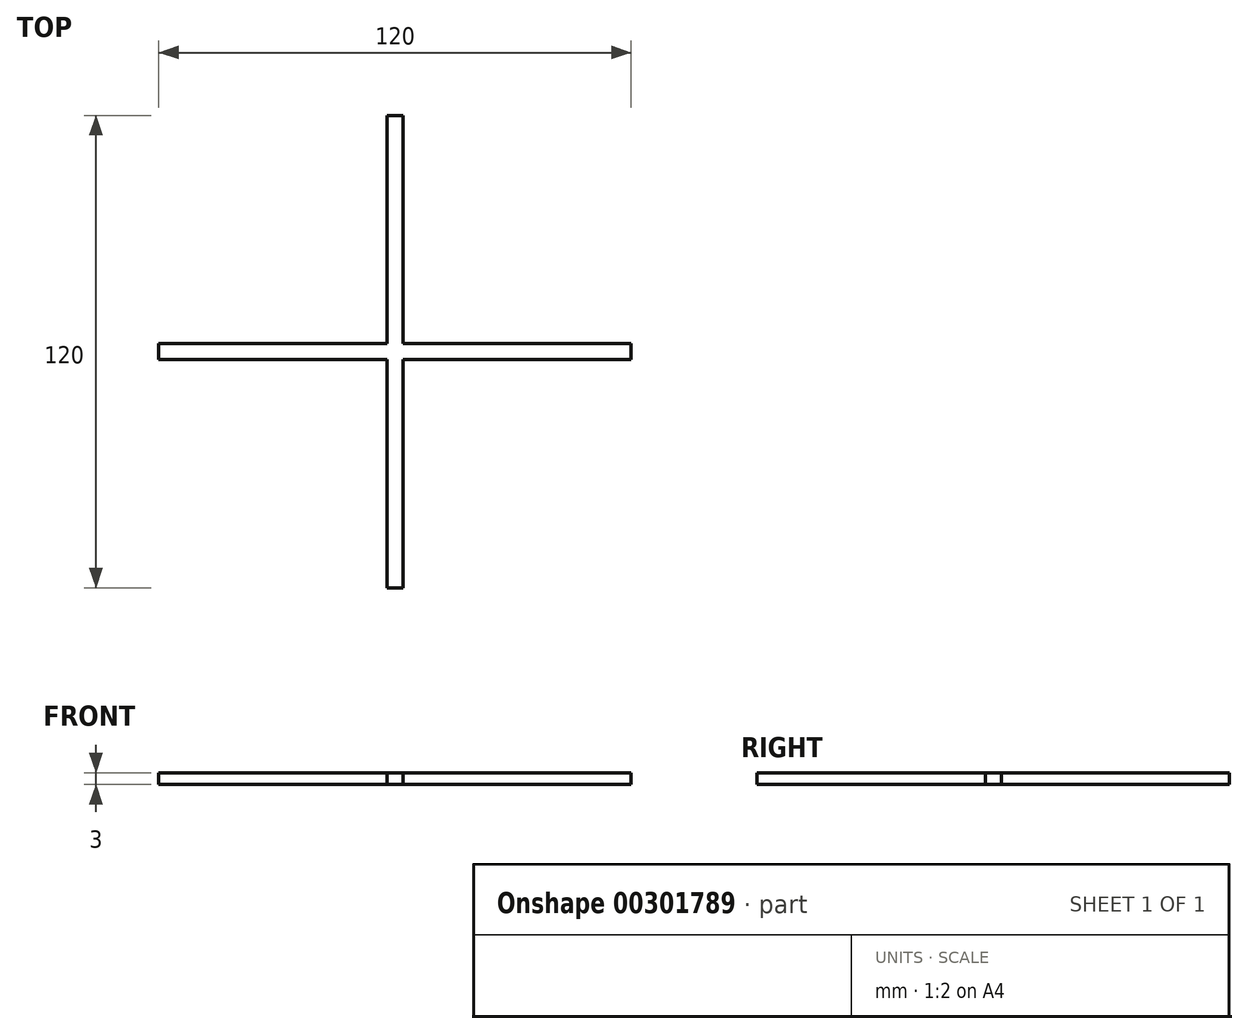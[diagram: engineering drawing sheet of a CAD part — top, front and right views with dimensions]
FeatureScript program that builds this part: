
annotation { "Feature Type Name" : "Feature", "Feature Type Description" : "" }
export const myFeature = defineFeature(function(context is Context, id is Id, definition is map)
    precondition{}
    {
        {
            var Q0;
            Q0=qCreatedBy(makeId("Top.planeOp"),FACE);
            var sketch = newSketch(context, id + "F0", { "sketchPlane" : qUnion([Q0])});
            skLineSegment(sketch, "E0.bottom", {"start": v(2, -60) * mm, "end": v(-2, -60) * mm});
            skLineSegment(sketch, "E0.top", {"start": v(2, 60) * mm, "end": v(-2, 60) * mm});
            skLineSegment(sketch, "E0.left", {"start": v(2, -60) * mm, "end": v(2, 60) * mm});
            skLineSegment(sketch, "E0.right", {"start": v(-2, -60) * mm, "end": v(-2, 60) * mm});
            skPoint(sketch, "E0.middle", {"position": v(0, 0) * mm});
            skLineSegment(sketch, "E1.bottom", {"start": v(60, -2) * mm, "end": v(-60, -2) * mm});
            skLineSegment(sketch, "E1.top", {"start": v(60, 2) * mm, "end": v(-60, 2) * mm});
            skLineSegment(sketch, "E1.left", {"start": v(60, -2) * mm, "end": v(60, 2) * mm});
            skLineSegment(sketch, "E1.right", {"start": v(-60, -2) * mm, "end": v(-60, 2) * mm});
            skSolve(sketch);
        }
        {
            var Q0;
            {var subQ5=sQuery(id+"F0.wireOp",EDGE,"E1.right");Q0=makeQuery(id+"F0.imprint","IMPRINT",FACE,{"disambiguationData":[TD([[makeQuery(id+"F0.imprint","IMPRINT",EDGE,{"derivedFrom":subQ5}),-1.0]])]});}
            var Q1;
            {var subQ0=sQuery(id+"F0.wireOp",EDGE,"E0.bottom");Q1=makeQuery(id+"F0.imprint","IMPRINT",FACE,{"disambiguationData":[TD([[makeQuery(id+"F0.imprint","IMPRINT",EDGE,{"derivedFrom":subQ0}),-1.0]])]});}
            var Q2;
            {var subQ0=sQuery(id+"F0.wireOp",EDGE,"E1.bottom");var subQ1=sQuery(id+"F0.wireOp",EDGE,"E0.left");var subQ2=makeQuery(id+"F0.imprint","INTERSECT",VERTEX,{"derivedFrom":[subQ1,subQ0]});Q2=makeQuery(id+"F0.imprint","IMPRINT",FACE,{"disambiguationData":[TD([[makeQuery(id+"F0.imprint","IMPRINT",EDGE,{"disambiguationData":[TD([[subQ2,-1.0]])],"derivedFrom":subQ1}),1.0]])]});}
            var Q3;
            {var subQ0=sQuery(id+"F0.wireOp",EDGE,"E0.top");Q3=makeQuery(id+"F0.imprint","IMPRINT",FACE,{"disambiguationData":[TD([[makeQuery(id+"F0.imprint","IMPRINT",EDGE,{"derivedFrom":subQ0}),1.0]])]});}
            var Q4;
            {var subQ5=sQuery(id+"F0.wireOp",EDGE,"E1.left");Q4=makeQuery(id+"F0.imprint","IMPRINT",FACE,{"disambiguationData":[TD([[makeQuery(id+"F0.imprint","IMPRINT",EDGE,{"derivedFrom":subQ5}),1.0]])]});}
            extrude(context, id + "F1", {"entities" : qUnion([Q0, Q1, Q2, Q3, Q4]), "depth" : 3 * mm});
        }
    });
